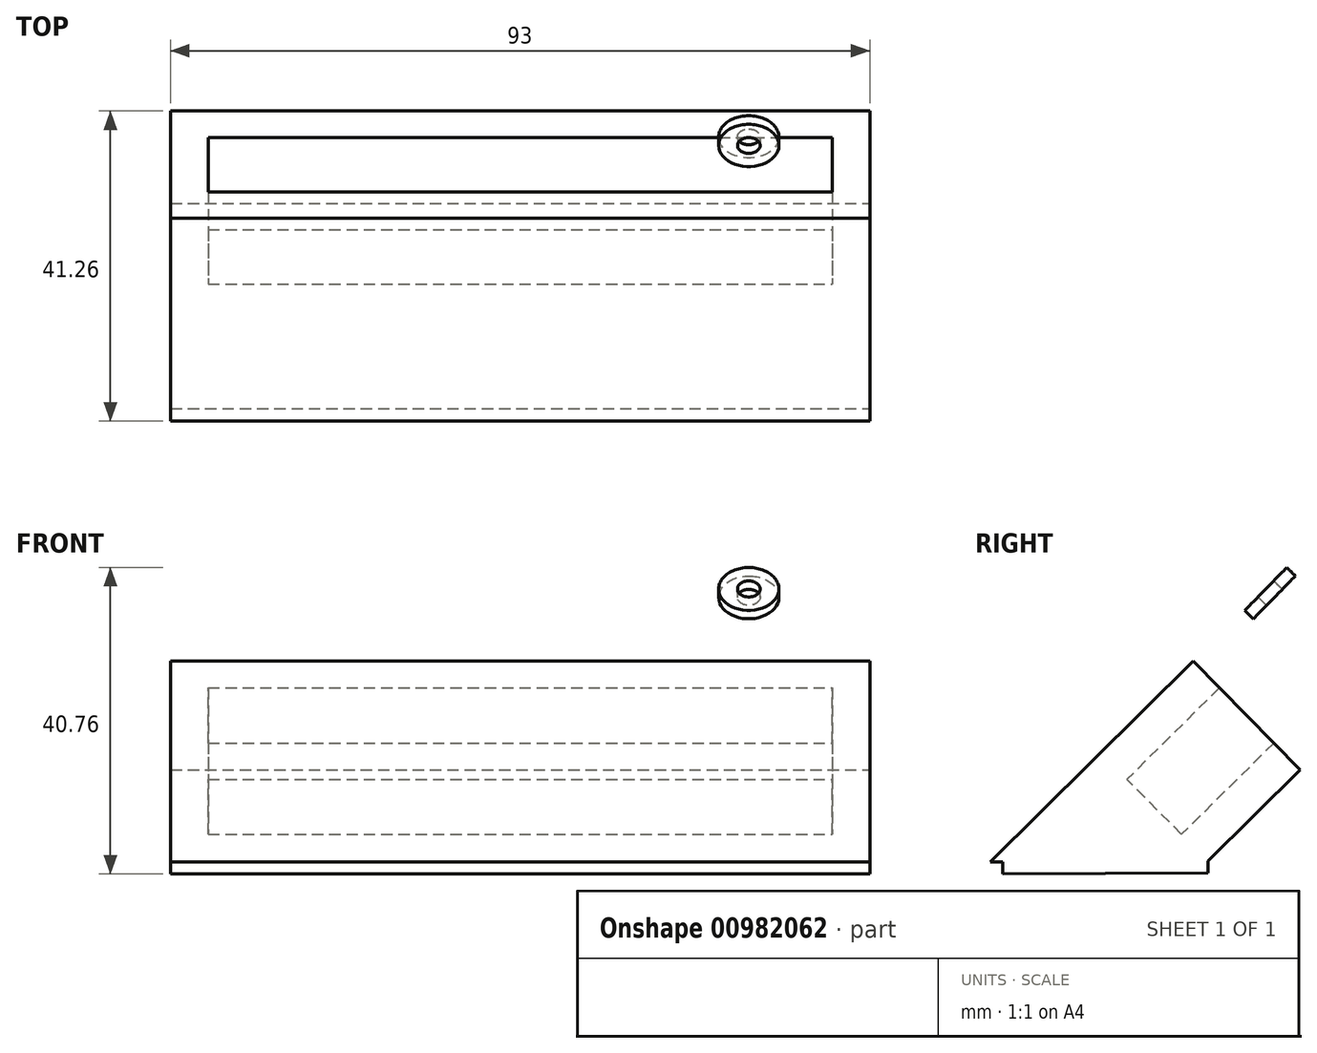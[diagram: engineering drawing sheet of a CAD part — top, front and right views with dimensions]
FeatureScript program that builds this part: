
annotation { "Feature Type Name" : "Feature", "Feature Type Description" : "" }
export const myFeature = defineFeature(function(context is Context, id is Id, definition is map)
    precondition{}
    {
        {
            var Q0;
            Q0=qCreatedBy(makeId("Top.planeOp"),FACE);
            var sketch = newSketch(context, id + "F0", { "sketchPlane" : qUnion([Q0])});
            skLineSegment(sketch, "E0.bottom", {"start": v(-28.31, 8.12) * mm, "end": v(54.69, 8.12) * mm});
            skLineSegment(sketch, "E0.top", {"start": v(-28.31, -2.18) * mm, "end": v(54.69, -2.18) * mm});
            skLineSegment(sketch, "E0.left", {"start": v(-28.31, 8.12) * mm, "end": v(-28.31, -2.18) * mm});
            skLineSegment(sketch, "E0.right", {"start": v(54.69, 8.12) * mm, "end": v(54.69, -2.18) * mm});
            skLineSegment(sketch, "E1.0", {"start": v(-33.31, 13.12) * mm, "end": v(59.69, 13.12) * mm});
            skLineSegment(sketch, "E1.1", {"start": v(-33.31, 13.12) * mm, "end": v(-33.31, -7.18) * mm});
            skLineSegment(sketch, "E1.2", {"start": v(-33.31, -7.18) * mm, "end": v(59.69, -7.18) * mm});
            skLineSegment(sketch, "E1.3", {"start": v(59.69, 13.12) * mm, "end": v(59.69, -7.18) * mm});
            skSolve(sketch);
        }
        {
            var Q0;
            Q0=makeQuery(id+"F0.imprint","IMPRINT",FACE,{"disambiguationData":[TD([[makeQuery(id+"F0.imprint","IMPRINT",EDGE,{"derivedFrom":sQuery(id+"F0.wireOp",EDGE,"E0.bottom")}),1.0]])]});
            extrude(context, id + "F1", {"entities" : qUnion([Q0]), "depth" : 17.3 * mm, "offsetDistance" : 25 * mm});
        }
        {
            var Q0;
            Q0=makeQuery(id+"F0.imprint","IMPRINT",FACE,{"disambiguationData":[TD([[makeQuery(id+"F0.imprint","IMPRINT",EDGE,{"derivedFrom":sQuery(id+"F0.wireOp",EDGE,"E0.bottom")}),-1.0]])]});
            var Q1;
            Q1=makeQuery(id+"F0.imprint","IMPRINT",FACE,{"disambiguationData":[TD([[makeQuery(id+"F0.imprint","IMPRINT",EDGE,{"derivedFrom":sQuery(id+"F0.wireOp",EDGE,"E0.bottom")}),1.0]])]});
            extrude(context, id + "F2", {"entities" : qUnion([Q0, Q1]), "operationType" : NewBodyOperationType.ADD, "oppositeDirection" : true, "depth" : 21.8 * mm, "offsetDistance" : 25 * mm});
        }
        {
            var Q0;
            {var subQ0=sQuery(id+"F0.wireOp",EDGE,"E1.3");Q0=makeQuery(id+"F2.boolean.opBoolean","MERGE",FACE,{"derivedFrom":[makeQuery(id+"F1.opExtrude","SWEPT_FACE",FACE,{"disambiguationData":[OSD([subQ0])]}),makeQuery(id+"F2.opExtrude","SWEPT_FACE",FACE,{"disambiguationData":[OSD([subQ0])]})]});}
            var sketch = newSketch(context, id + "F3", { "sketchPlane" : qUnion([Q0])});
            skLineSegment(sketch, "E2", {"start": v(13.12, 0) * mm, "end": v(-6.02, -19.48) * mm});
            skLineSegment(sketch, "E3", {"start": v(-7.18, 0) * mm, "end": v(-7.18, -19.94) * mm});
            skLineSegment(sketch, "E4", {"start": v(-7.18, -19.94) * mm, "end": v(-7.18, -22.02) * mm});
            skLineSegment(sketch, "E5", {"start": v(-6.02, -19.48) * mm, "end": v(-7.18, -20.66) * mm});
            skLineSegment(sketch, "E6", {"start": v(13.12, 0) * mm, "end": v(14.73, 0) * mm});
            skLineSegment(sketch, "E7", {"start": v(14.73, 0) * mm, "end": v(14.73, -23.39) * mm});
            skLineSegment(sketch, "E8", {"start": v(14.73, -23.39) * mm, "end": v(-7.18, -23.39) * mm});
            skLineSegment(sketch, "E9", {"start": v(-7.18, -23.39) * mm, "end": v(-7.18, -20.66) * mm});
            skSolve(sketch);
        }
        {
            var Q0;
            {var subQ4=sQuery(id+"F3.wireOp",EDGE,"E2");Q0=makeQuery(id+"F3.imprint","IMPRINT",FACE,{"disambiguationData":[TD([[makeQuery(id+"F3.imprint","IMPRINT",EDGE,{"derivedFrom":subQ4}),1.0]])]});}
            var Q1;
            {var subQ4=sQuery(id+"F3.wireOp",EDGE,"E6");Q1=makeQuery(id+"F3.imprint","IMPRINT",FACE,{"disambiguationData":[TD([[makeQuery(id+"F3.imprint","IMPRINT",EDGE,{"derivedFrom":subQ4}),-1.0]])]});}
            extrude(context, id + "F4", {"entities" : qUnion([Q0, Q1]), "operationType" : NewBodyOperationType.REMOVE, "oppositeDirection" : true, "depth" : 95.7 * mm, "offsetDistance" : 25 * mm});
        }
        {
            var Q0;
            Q0=makeQuery(id+"F4.boolean.opBoolean","COPY",FACE,{"derivedFrom":makeQuery(id+"F4.opExtrude","SWEPT_FACE",FACE,{"disambiguationData":[OSD([sQuery(id+"F3.wireOp",EDGE,"E2"),sQuery(id+"F3.wireOp",EDGE,"E5")])]})});
            var sketch = newSketch(context, id + "F5", { "sketchPlane" : qUnion([Q0])});
            skLineSegment(sketch, "E10", {"start": v(-54.69, 33.46) * mm, "end": v(33.31, 33.46) * mm});
            skCircle(sketch, "E11", {"center": v(-43.59, 33.46) * mm, "radius": 1.5 * mm});
            skCircle(sketch, "E12", {"center": v(-43.59, 33.46) * mm, "radius": 4 * mm});
            skPoint(sketch, "E13.visualSharp", {"position": v(-59.69, 33.46) * mm});
            skLineSegment(sketch, "E14", {"start": v(-54.69, 33.46) * mm, "end": v(-59.69, 33.46) * mm});
            skLineSegment(sketch, "E15", {"start": v(-59.69, 33.46) * mm, "end": v(-59.69, 14.2) * mm});
            skLineSegment(sketch, "E16.bottom", {"start": v(-59.69, 33.46) * mm, "end": v(33.31, 33.46) * mm});
            skLineSegment(sketch, "E16.top", {"start": v(-59.69, -1.53) * mm, "end": v(33.31, -1.53) * mm});
            skLineSegment(sketch, "E16.left", {"start": v(-59.69, 33.46) * mm, "end": v(-59.69, -1.53) * mm});
            skLineSegment(sketch, "E16.right", {"start": v(33.31, 33.46) * mm, "end": v(33.31, -1.53) * mm});
            skCircle(sketch, "E17", {"center": v(16.9, 33.46) * mm, "radius": 1.5 * mm});
            skCircle(sketch, "E18", {"center": v(16.9, 33.46) * mm, "radius": 4 * mm});
            skLineSegment(sketch, "E19", {"start": v(-45.77, 36.82) * mm, "end": v(-50.92, 33.46) * mm});
            skLineSegment(sketch, "E20", {"start": v(-41.4, 36.82) * mm, "end": v(-35.32, 33.46) * mm});
            skLineSegment(sketch, "E21", {"start": v(14.72, 36.82) * mm, "end": v(9.9, 33.46) * mm});
            skLineSegment(sketch, "E22", {"start": v(19.08, 36.82) * mm, "end": v(24.24, 33.46) * mm});
            skSolve(sketch);
        }
        {
            var Q0;
            {var subQ5=makeQuery(id+"F4.boolean.opBoolean","COPY",EDGE,{"derivedFrom":makeQuery(id+"F4.opExtrude","SWEPT_EDGE",EDGE,{"disambiguationData":[OSD([sQuery(id+"F0.wireOp",EDGE,"E1.0"),sQuery(id+"F0.wireOp",EDGE,"E1.3"),sQuery(id+"F3.wireOp",EDGE,"E2"),sQuery(id+"F3.wireOp",EDGE,"E6")])]})});Q0=makeQuery(id+"F5.imprint","IMPRINT",FACE,{"disambiguationData":[TD([[makeQuery(id+"F5.imprint","IMPRINT",EDGE,{"derivedFrom":subQ5}),-1.0]])]});}
            var Q1;
            {var subQ0=sQuery(id+"F5.wireOp",EDGE,"E16.top");Q1=makeQuery(id+"F5.imprint","IMPRINT",FACE,{"disambiguationData":[TD([[makeQuery(id+"F5.imprint","IMPRINT",EDGE,{"derivedFrom":subQ0}),1.0]])]});}
            var Q2;
            {var subQ0=sQuery(id+"F5.wireOp",EDGE,"E16.top");Q2=makeQuery(id+"F5.imprint","IMPRINT",FACE,{"disambiguationData":[TD([[makeQuery(id+"F5.imprint","IMPRINT",EDGE,{"derivedFrom":subQ0}),-1.0]])]});}
            var Q3;
            {var subQ0=sQuery(id+"F5.wireOp",EDGE,"E16.bottom");var subQ1=sQuery(id+"F5.wireOp",EDGE,"E11");var subQ2=makeQuery(id+"F5.imprint","INTERSECT",VERTEX,{"disambiguationData":[OD(0.0)],"derivedFrom":[subQ1,subQ0]});Q3=makeQuery(id+"F5.imprint","IMPRINT",FACE,{"disambiguationData":[TD([[makeQuery(id+"F5.imprint","IMPRINT",EDGE,{"disambiguationData":[TD([[subQ2,1.0]])],"derivedFrom":subQ1}),-1.0]])]});}
            var Q4;
            {var subQ0=sQuery(id+"F5.wireOp",EDGE,"E18");var subQ1=sQuery(id+"F5.wireOp",EDGE,"E16.bottom");var subQ2=makeQuery(id+"F5.imprint","INTERSECT",VERTEX,{"disambiguationData":[OD(0.0)],"derivedFrom":[subQ1,subQ0]});Q4=makeQuery(id+"F5.imprint","IMPRINT",FACE,{"disambiguationData":[TD([[makeQuery(id+"F5.imprint","IMPRINT",EDGE,{"disambiguationData":[TD([[subQ2,-1.0]])],"derivedFrom":subQ1}),1.0]])]});}
            var Q5;
            {var subQ0=sQuery(id+"F5.wireOp",EDGE,"E19");Q5=makeQuery(id+"F5.imprint","IMPRINT",FACE,{"disambiguationData":[TD([[makeQuery(id+"F5.imprint","IMPRINT",EDGE,{"derivedFrom":subQ0}),1.0]])]});}
            var Q6;
            {var subQ0=sQuery(id+"F5.wireOp",EDGE,"E20");Q6=makeQuery(id+"F5.imprint","IMPRINT",FACE,{"disambiguationData":[TD([[makeQuery(id+"F5.imprint","IMPRINT",EDGE,{"derivedFrom":subQ0}),-1.0]])]});}
            var Q7;
            {var subQ0=sQuery(id+"F5.wireOp",EDGE,"E21");var subQ1=sQuery(id+"F5.wireOp",EDGE,"E16.bottom");var subQ2=makeQuery(id+"F5.imprint","INTERSECT",VERTEX,{"derivedFrom":[subQ1,subQ0]});Q7=makeQuery(id+"F5.imprint","IMPRINT",FACE,{"disambiguationData":[TD([[makeQuery(id+"F5.imprint","IMPRINT",EDGE,{"disambiguationData":[TD([[subQ2,-1.0]])],"derivedFrom":subQ1}),1.0]])]});}
            var Q8;
            {var subQ0=sQuery(id+"F5.wireOp",EDGE,"E22");Q8=makeQuery(id+"F5.imprint","IMPRINT",FACE,{"disambiguationData":[TD([[makeQuery(id+"F5.imprint","IMPRINT",EDGE,{"derivedFrom":subQ0}),-1.0]])]});}
            var Q9;
            {var subQ0=sQuery(id+"F5.wireOp",EDGE,"E16.bottom");var subQ1=sQuery(id+"F5.wireOp",EDGE,"E11");var subQ2=makeQuery(id+"F5.imprint","INTERSECT",VERTEX,{"disambiguationData":[OD(0.0)],"derivedFrom":[subQ1,subQ0]});Q9=makeQuery(id+"F5.imprint","IMPRINT",FACE,{"disambiguationData":[TD([[makeQuery(id+"F5.imprint","IMPRINT",EDGE,{"disambiguationData":[TD([[subQ2,-1.0]])],"derivedFrom":subQ1}),-1.0]])]});}
            var Q10;
            {var subQ0=sQuery(id+"F5.wireOp",EDGE,"E18");var subQ1=sQuery(id+"F5.wireOp",EDGE,"E16.bottom");var subQ2=makeQuery(id+"F5.imprint","INTERSECT",VERTEX,{"disambiguationData":[OD(0.0)],"derivedFrom":[subQ1,subQ0]});Q10=makeQuery(id+"F5.imprint","IMPRINT",FACE,{"disambiguationData":[TD([[makeQuery(id+"F5.imprint","IMPRINT",EDGE,{"disambiguationData":[TD([[subQ2,-1.0]])],"derivedFrom":subQ1}),-1.0]])]});}
            extrude(context, id + "F6", {"entities" : qUnion([Q0, Q1, Q2, Q3, Q4, Q5, Q6, Q7, Q8, Q9, Q10]), "operationType" : NewBodyOperationType.ADD, "depth" : 1.6 * mm, "offsetDistance" : 25 * mm});
        }
        {
            var Q0;
            Q0=makeQuery(id+"F1.opExtrude","SWEPT_BODY",BODY,{"disambiguationData":[OSD([sQuery(id+"F0.wireOp",EDGE,"E0.bottom"),sQuery(id+"F0.wireOp",EDGE,"E0.top"),sQuery(id+"F0.wireOp",EDGE,"E0.left"),sQuery(id+"F0.wireOp",EDGE,"E0.right"),sQuery(id+"F0.wireOp",EDGE,"E1.0"),sQuery(id+"F0.wireOp",EDGE,"E1.1"),sQuery(id+"F0.wireOp",EDGE,"E1.2"),sQuery(id+"F0.wireOp",EDGE,"E1.3")])]});
            var Q1;
            Q1=makeQuery(id+"F6.opExtrude","CAP_EDGE",EDGE,{"disambiguationData":[OSD([sQuery(id+"F3.wireOp",EDGE,"E4"),sQuery(id+"F3.wireOp",EDGE,"E5"),sQuery(id+"F3.wireOp",EDGE,"E9")])],"isStart":false});
            transform(context, id + "F7", {"entities" : qUnion([Q0]), "transformType" : TransformType.ROTATION, "transformAxis" : qUnion([Q1]), "angle" : 45.3 * degree, "oppositeDirection" : true, "makeCopy" : false});
        }
    });
